# Revit family: 304_d79798b26e5549ed86ae19a5024990
name_source: partatom
category: Pipe Accessories
units: mm (PartAtom-declared; Revit-internal decimal feet)

## family parameters
Always vertical = Yes
Cut with Voids When Loaded = No
Part Type = Valve - Breaks Into
Round Connector Dimension = Use Diameter
Shared = No
Work Plane-Based = No

## types (7) — shared parameters
CAT0 = Yes
Description = Automatic balancing valve
L2D = 69 mm
L2D_Min = 3048 mm
Manufacturer = Frese A/S
QmdConnectorList = 301;D;302;D
URL = https://www.frese.eu
W2D = 15 mm  [stored 0.0492126 ft]
magiPartTypeId = 304
magiProductFamilyId = d79798b26e5549ed86ae19a5024990

## per-type parameters (varying)
| type | D | D2 | D32 | D4 | D42 | D5 | D6 | H1 | H2 | H2__ve | H3 | H4 | H5 | H6 | L1 | L1__ve | L2 | L3 | L4 | LL | S | magiProductId |
| Frese ALPHA DN15 HP with P/T plugs | 15 mm | 29 mm  [stored 0.0951444 ft] | 11 mm | 17 mm | 6 mm  [stored 0.019685 ft] | 18 mm  [stored 0.0590551 ft] | 14 mm  [stored 0.0459318 ft] | 27 mm  [stored 0.0885827 ft] | 75 mm | -75 mm | 8 mm  [stored 0.0262467 ft] | 59 mm | 80 mm | 21 mm  [stored 0.0688976 ft] | 17 mm | -17 mm | 35 mm | 2 mm  [stored 0.00656168 ft] | 26 mm  [stored 0.0853018 ft] | 35 mm | 23 mm  [stored 0.0754593 ft] | dd04ccff6b8c4abdbc2c4650cce179 |
| Frese ALPHA DN20 HP with P/T plugs | 20 mm | 39 mm  [stored 0.127953 ft] | 14 mm  [stored 0.0459318 ft] | 22 mm  [stored 0.0721785 ft] | 9 mm  [stored 0.0295276 ft] | 23 mm  [stored 0.0754593 ft] | 19 mm  [stored 0.062336 ft] | 33 mm  [stored 0.108268 ft] | 75 mm | -75 mm | 8 mm  [stored 0.0262467 ft] | 59 mm | 80 mm | 21 mm  [stored 0.0688976 ft] | 19 mm  [stored 0.062336 ft] | -19 mm | 39 mm  [stored 0.127953 ft] | 4 mm  [stored 0.0131234 ft] | 29 mm  [stored 0.0951444 ft] | 39 mm  [stored 0.127953 ft] | 30 mm  [stored 0.0984252 ft] | 2711600c8a5940cabaa2c3ea414958 |
| Frese ALPHA DN25 HP with P/T plugs | 25 mm | 39 mm  [stored 0.127953 ft] | 14 mm  [stored 0.0459318 ft] | 28 mm  [stored 0.0918635 ft] | 12 mm  [stored 0.0393701 ft] | 24 mm  [stored 0.0787402 ft] | 19 mm  [stored 0.062336 ft] | 36 mm  [stored 0.11811 ft] | 75 mm | -75 mm | 8 mm  [stored 0.0262467 ft] | 59 mm | 80 mm | 21 mm  [stored 0.0688976 ft] | 21 mm  [stored 0.0688976 ft] | -21 mm | 42 mm | 4 mm  [stored 0.0131234 ft] | 31 mm | 42 mm | 38 mm  [stored 0.124672 ft] | b41c5e33a1de4a96a82b9009714bae |
| Frese ALPHA DN25L HP with P/T plugs | 25 mm | 39 mm  [stored 0.127953 ft] | 14 mm  [stored 0.0459318 ft] | 28 mm  [stored 0.0918635 ft] | 12 mm  [stored 0.0393701 ft] | 24 mm  [stored 0.0787402 ft] | 19 mm  [stored 0.062336 ft] | 40 mm | 102 mm | -102 mm | 11 mm | 77 mm | 107 mm | 30 mm  [stored 0.0984252 ft] | 29 mm  [stored 0.0951444 ft] | -29 mm | 58 mm | 1 mm  [stored 0.00328084 ft] | 42 mm | 58 mm | 38 mm  [stored 0.124672 ft] | 0e23e4a20e5d425382f06a4b5ad0bb |
| Frese ALPHA DN32 HP with P/T plugs | 32 mm | 48 mm | 14 mm  [stored 0.0459318 ft] | 35 mm | 16 mm  [stored 0.0524934 ft] | 29 mm  [stored 0.0951444 ft] | 19 mm  [stored 0.062336 ft] | 46 mm | 102 mm | -102 mm | 11 mm | 77 mm | 107 mm | 30 mm  [stored 0.0984252 ft] | 29 mm  [stored 0.0951444 ft] | -29 mm | 57 mm | 2 mm  [stored 0.00656168 ft] | 42 mm | 57 mm | 48 mm | fd4f625f171241ebbad4a3060240b8 |
| Frese ALPHA DN40 HP with P/T plugs | 40 mm | 56 mm | 17 mm | 44 mm | 20 mm  [stored 0.0656168 ft] | 34 mm  [stored 0.111549 ft] | 22 mm  [stored 0.0721785 ft] | 53 mm | 102 mm | -102 mm | 11 mm | 77 mm | 107 mm | 30 mm  [stored 0.0984252 ft] | 29 mm  [stored 0.0951444 ft] | -29 mm | 57 mm | 6 mm  [stored 0.019685 ft] | 42 mm | 57 mm | 56 mm | 5c6780ae6f6e4cfaa0bb9a07a9c7ea |
| Frese ALPHA DN50 HP with P/T plugs | 50 mm | 60 mm | 18 mm  [stored 0.0590551 ft] | 55 mm | 26 mm  [stored 0.0853018 ft] | 36 mm  [stored 0.11811 ft] | 24 mm  [stored 0.0787402 ft] | 59 mm | 102 mm | -102 mm | 11 mm | 77 mm | 107 mm | 30 mm  [stored 0.0984252 ft] | 32 mm  [stored 0.104987 ft] | -32 mm | 65 mm | 5 mm  [stored 0.0164042 ft] | 47 mm | 65 mm | 60 mm | f45b976efe734fa286e553cc50064e |

note: column(s) folded — value = type name in every type: MC Product Code

note: [stored X ft] marks values corroborated as IEEE doubles in the binary element streams (Revit-internal decimal feet)

## geometry (parser evidence)
native form markers: Sweep x1
no freeform markers — native parametric forms only
